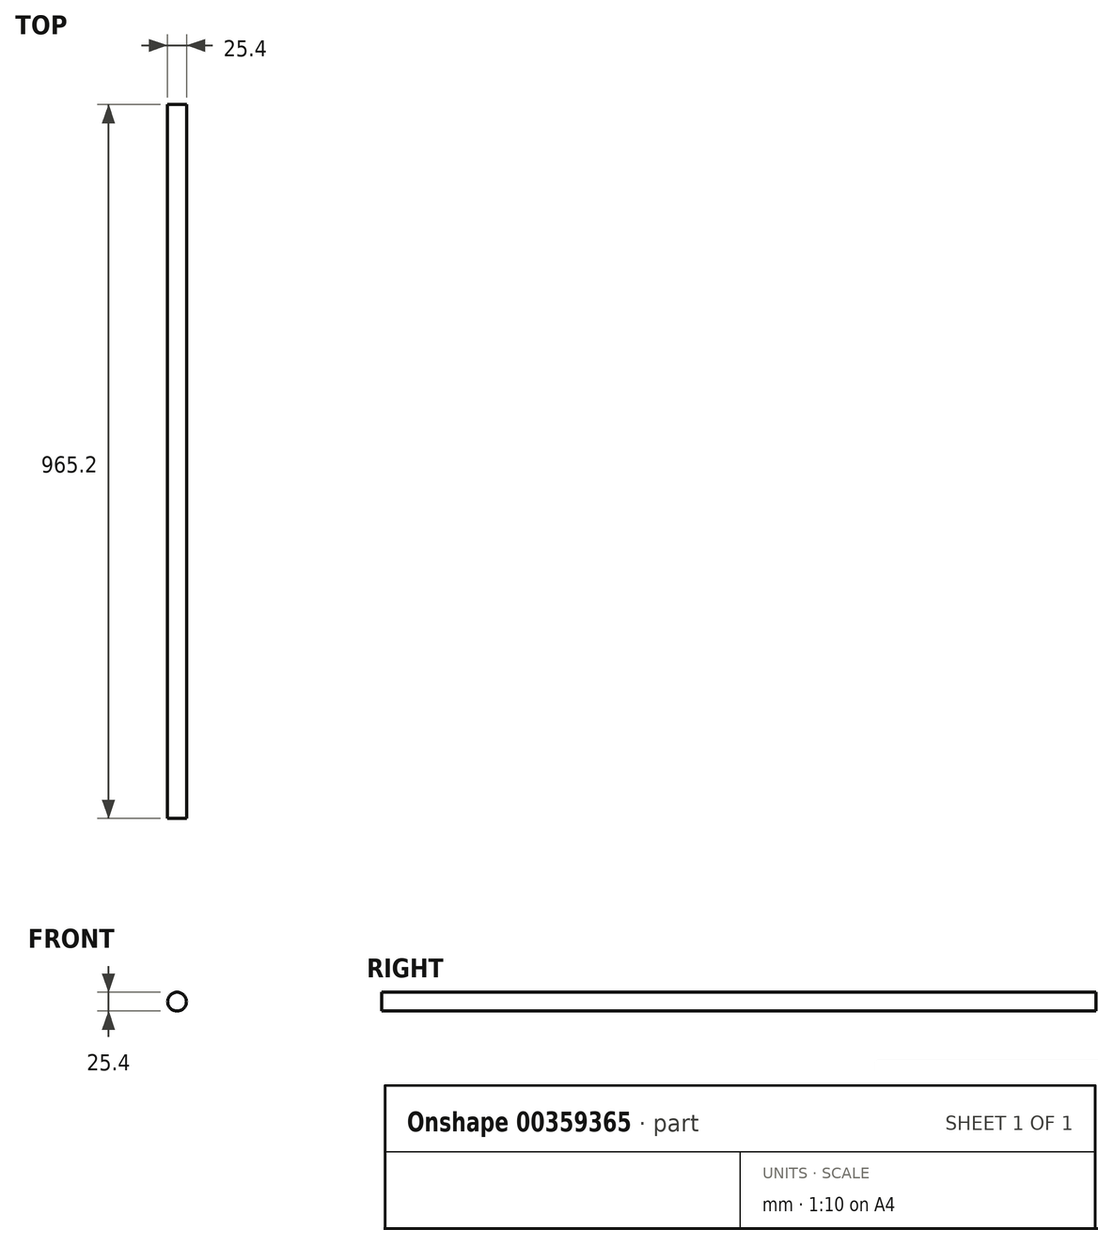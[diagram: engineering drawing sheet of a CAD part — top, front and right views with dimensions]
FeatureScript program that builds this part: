
annotation { "Feature Type Name" : "Feature", "Feature Type Description" : "" }
export const myFeature = defineFeature(function(context is Context, id is Id, definition is map)
    precondition{}
    {
        {
            var Q0;
            Q0=qCreatedBy(makeId("Front.planeOp"),FACE);
            var sketch = newSketch(context, id + "F0", { "sketchPlane" : qUnion([Q0])});
            skCircle(sketch, "E0", {"center": v(0, 0) * mm, "radius": 12.7 * mm});
            skSolve(sketch);
        }
        {
            var Q0;
            Q0=makeQuery(id+"F0.imprint","IMPRINT",FACE,{"disambiguationData":[TD([[makeQuery(id+"F0.imprint","IMPRINT",EDGE,{"derivedFrom":sQuery(id+"F0.wireOp",EDGE,"E0")}),1.0]])]});
            extrude(context, id + "F1", {"entities" : qUnion([Q0]), "depth" : 965.2 * mm, "offsetDistance" : 25.4 * mm});
        }
    });
